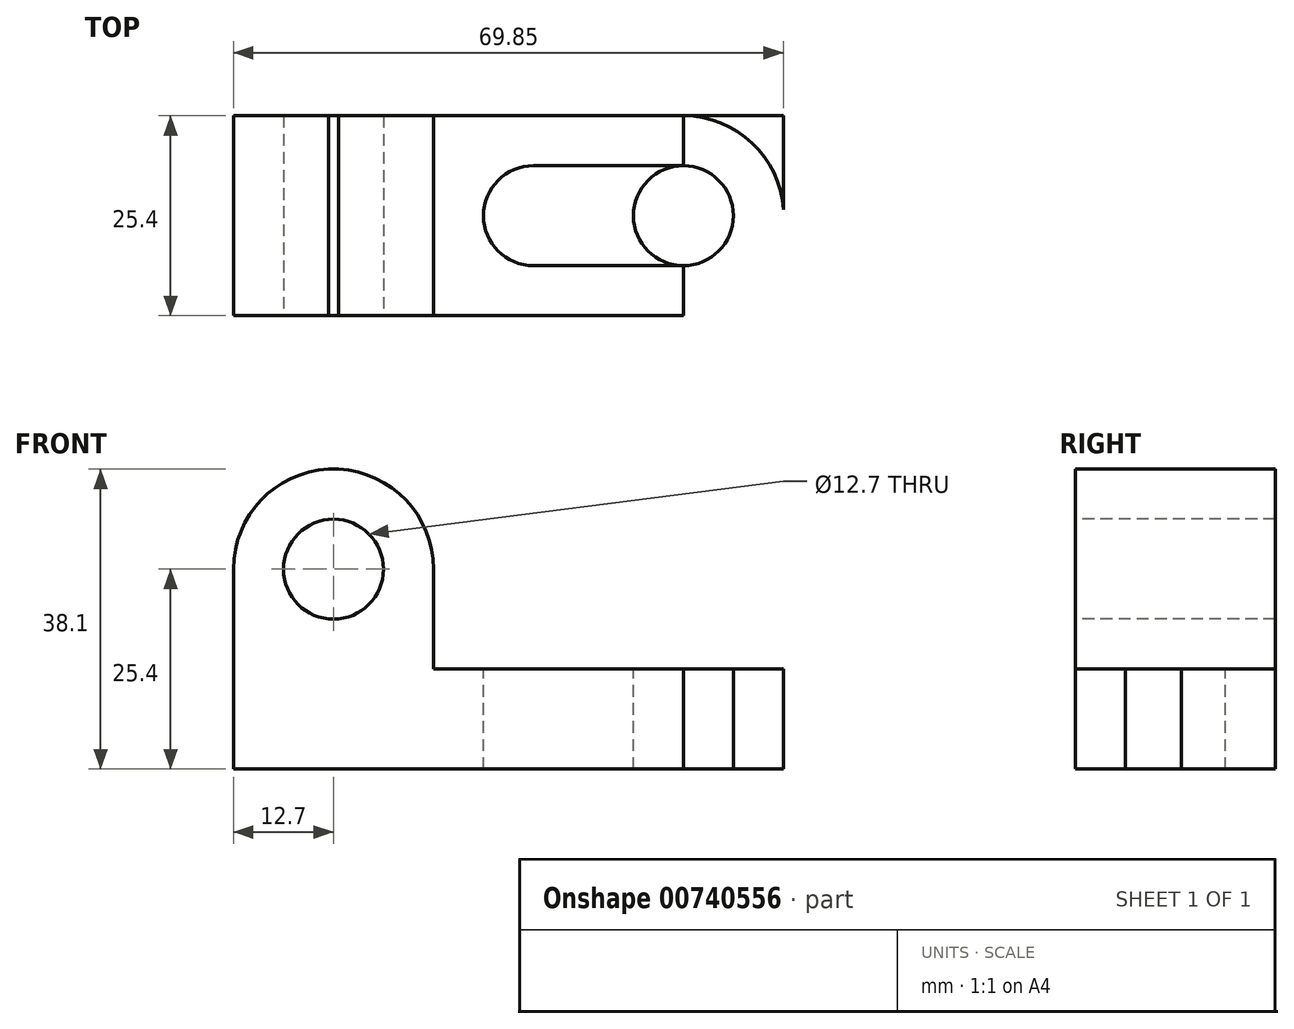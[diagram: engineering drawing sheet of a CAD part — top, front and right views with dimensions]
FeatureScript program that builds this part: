
annotation { "Feature Type Name" : "Feature", "Feature Type Description" : "" }
export const myFeature = defineFeature(function(context is Context, id is Id, definition is map)
    precondition{}
    {
        {
            var Q0;
            Q0=qCreatedBy(makeId("Front.planeOp"),FACE);
            var sketch = newSketch(context, id + "F0", { "sketchPlane" : qUnion([Q0])});
            skLineSegment(sketch, "E0", {"start": v(0, 0) * mm, "end": v(0, 38.1) * mm});
            skLineSegment(sketch, "E1", {"start": v(0, 38.1) * mm, "end": v(25.4, 38.1) * mm});
            skLineSegment(sketch, "E2", {"start": v(25.4, 38.1) * mm, "end": v(25.4, 12.7) * mm});
            skLineSegment(sketch, "E3", {"start": v(25.4, 12.7) * mm, "end": v(69.85, 12.7) * mm});
            skLineSegment(sketch, "E4", {"start": v(69.85, 12.7) * mm, "end": v(69.85, 0) * mm});
            skLineSegment(sketch, "E5", {"start": v(69.85, 0) * mm, "end": v(0, 0) * mm});
            skSolve(sketch);
        }
        {
            var Q0;
            Q0 = qSketchRegion(id + "F0", true);
            extrude(context, id + "F1", {"entities" : qUnion([Q0]), "depth" : 25.4 * mm, "offsetDistance" : 25.4 * mm});
        }
        {
            var Q0;
            Q0=makeQuery(id+"F1.opExtrude","CAP_FACE",FACE,{"disambiguationData":[OSD([sQuery(id+"F0.wireOp",EDGE,"E0"),sQuery(id+"F0.wireOp",EDGE,"E1"),sQuery(id+"F0.wireOp",EDGE,"E2"),sQuery(id+"F0.wireOp",EDGE,"E3"),sQuery(id+"F0.wireOp",EDGE,"E4"),sQuery(id+"F0.wireOp",EDGE,"E5")])],"isStart":false});
            var sketch = newSketch(context, id + "F2", { "sketchPlane" : qUnion([Q0])});
            skLineSegment(sketch, "E6", {"start": v(0, 25.4) * mm, "end": v(25.4, 25.4) * mm});
            skCircle(sketch, "E7", {"center": v(12.7, 25.4) * mm, "radius": 6.35 * mm});
            skArc(sketch, "E8", {"start": v(25.4, 25.4) * mm, "mid": v(12.7, 38.12) * mm, "end": v(0, 25.4) * mm});
            skSolve(sketch);
        }
        {
            var Q0;
            {var subQ0=sQuery(id+"F2.wireOp",EDGE,"E7");var subQ1=sQuery(id+"F2.wireOp",EDGE,"E6");var subQ2=makeQuery(id+"F2.imprint","INTERSECT",VERTEX,{"disambiguationData":[OD(0.0)],"derivedFrom":[subQ1,subQ0]});Q0=makeQuery(id+"F2.imprint","IMPRINT",FACE,{"disambiguationData":[TD([[makeQuery(id+"F2.imprint","IMPRINT",EDGE,{"disambiguationData":[TD([[subQ2,-1.0]])],"derivedFrom":subQ1}),1.0]])]});}
            var Q1;
            {var subQ0=sQuery(id+"F2.wireOp",EDGE,"E7");var subQ1=sQuery(id+"F2.wireOp",EDGE,"E6");var subQ2=makeQuery(id+"F2.imprint","INTERSECT",VERTEX,{"disambiguationData":[OD(0.0)],"derivedFrom":[subQ1,subQ0]});Q1=makeQuery(id+"F2.imprint","IMPRINT",FACE,{"disambiguationData":[TD([[makeQuery(id+"F2.imprint","IMPRINT",EDGE,{"disambiguationData":[TD([[subQ2,-1.0]])],"derivedFrom":subQ1}),-1.0]])]});}
            var Q2;
            {var subQ0=sQuery(id+"F2.wireOp",EDGE,"E8");var subQ3=makeQuery(id+"F1.opExtrude","CAP_EDGE",EDGE,{"disambiguationData":[OSD([sQuery(id+"F0.wireOp",EDGE,"E1")])],"isStart":false});var subQ4=makeQuery(id+"F2.imprint","INTERSECT",VERTEX,{"disambiguationData":[OD(1.0)],"derivedFrom":[subQ3,subQ0]});Q2=makeQuery(id+"F2.imprint","IMPRINT",FACE,{"disambiguationData":[TD([[makeQuery(id+"F2.imprint","IMPRINT",EDGE,{"disambiguationData":[TD([[subQ4,-1.0]])],"derivedFrom":subQ0}),-1.0]])]});}
            var Q3;
            {var subQ0=sQuery(id+"F2.wireOp",EDGE,"E8");var subQ3=makeQuery(id+"F1.opExtrude","CAP_EDGE",EDGE,{"disambiguationData":[OSD([sQuery(id+"F0.wireOp",EDGE,"E1")])],"isStart":false});var subQ4=makeQuery(id+"F2.imprint","INTERSECT",VERTEX,{"disambiguationData":[OD(0.0)],"derivedFrom":[subQ3,subQ0]});Q3=makeQuery(id+"F2.imprint","IMPRINT",FACE,{"disambiguationData":[TD([[makeQuery(id+"F2.imprint","IMPRINT",EDGE,{"disambiguationData":[TD([[subQ4,1.0]])],"derivedFrom":subQ0}),-1.0]])]});}
            extrude(context, id + "F3", {"entities" : qUnion([Q0, Q1, Q2, Q3]), "operationType" : NewBodyOperationType.REMOVE, "endBound" : BoundingType.THROUGH_ALL, "oppositeDirection" : true, "depth" : 25.4 * mm, "offsetDistance" : 25.4 * mm});
        }
        {
            var Q0;
            Q0=makeQuery(id+"F1.opExtrude","SWEPT_FACE",FACE,{"disambiguationData":[OSD([sQuery(id+"F0.wireOp",EDGE,"E3")])]});
            var sketch = newSketch(context, id + "F4", { "sketchPlane" : qUnion([Q0])});
            skLineSegment(sketch, "E9", {"start": v(38.1, 0) * mm, "end": v(38.1, -25.4) * mm});
            skLineSegment(sketch, "E10", {"start": v(57.15, 0) * mm, "end": v(57.15, -25.4) * mm});
            skCircle(sketch, "E11", {"center": v(38.1, -12.7) * mm, "radius": 6.35 * mm});
            skCircle(sketch, "E12", {"center": v(57.15, -12.7) * mm, "radius": 6.35 * mm});
            skLineSegment(sketch, "E13", {"start": v(38.1, -6.35) * mm, "end": v(57.15, -6.35) * mm});
            skLineSegment(sketch, "E14", {"start": v(57.15, -6.35) * mm, "end": v(57.15, -19.05) * mm});
            skLineSegment(sketch, "E15", {"start": v(57.15, -19.05) * mm, "end": v(38.1, -19.05) * mm});
            skArc(sketch, "E16", {"start": v(57.15, -25.4) * mm, "mid": v(69.87, -12.7) * mm, "end": v(57.15, 0) * mm});
            skSolve(sketch);
        }
        {
            var Q0;
            {var subQ0=sQuery(id+"F4.wireOp",EDGE,"E11");var subQ1=sQuery(id+"F4.wireOp",EDGE,"E9");var subQ2=makeQuery(id+"F4.imprint","INTERSECT",VERTEX,{"derivedFrom":[subQ1,subQ0,sQuery(id+"F4.wireOp",EDGE,"E13")]});Q0=makeQuery(id+"F4.imprint","IMPRINT",FACE,{"disambiguationData":[TD([[makeQuery(id+"F4.imprint","IMPRINT",EDGE,{"disambiguationData":[TD([[subQ2,-1.0]])],"derivedFrom":subQ1}),-1.0]])]});}
            var Q1;
            {var subQ0=sQuery(id+"F4.wireOp",EDGE,"E11");var subQ1=sQuery(id+"F4.wireOp",EDGE,"E9");var subQ2=makeQuery(id+"F4.imprint","INTERSECT",VERTEX,{"derivedFrom":[subQ1,subQ0,sQuery(id+"F4.wireOp",EDGE,"E13")]});Q1=makeQuery(id+"F4.imprint","IMPRINT",FACE,{"disambiguationData":[TD([[makeQuery(id+"F4.imprint","IMPRINT",EDGE,{"disambiguationData":[TD([[subQ2,-1.0]])],"derivedFrom":subQ1}),1.0]])]});}
            var Q2;
            {var subQ0=sQuery(id+"F4.wireOp",EDGE,"E14");Q2=makeQuery(id+"F4.imprint","IMPRINT",FACE,{"disambiguationData":[TD([[makeQuery(id+"F4.imprint","IMPRINT",EDGE,{"derivedFrom":subQ0}),-1.0]])]});}
            var Q3;
            {var subQ0=sQuery(id+"F4.wireOp",EDGE,"E14");Q3=makeQuery(id+"F4.imprint","IMPRINT",FACE,{"disambiguationData":[TD([[makeQuery(id+"F4.imprint","IMPRINT",EDGE,{"derivedFrom":subQ0}),1.0]])]});}
            var Q4;
            {var subQ0=sQuery(id+"F4.wireOp",EDGE,"E13");Q4=makeQuery(id+"F4.imprint","IMPRINT",FACE,{"disambiguationData":[TD([[makeQuery(id+"F4.imprint","IMPRINT",EDGE,{"derivedFrom":subQ0}),-1.0]])]});}
            var Q5;
            {var subQ0=sQuery(id+"F4.wireOp",EDGE,"E16");var subQ1=makeQuery(id+"F1.opExtrude","SWEPT_EDGE",EDGE,{"disambiguationData":[OSD([sQuery(id+"F0.wireOp",EDGE,"E3"),sQuery(id+"F0.wireOp",EDGE,"E4")])]});var subQ2=makeQuery(id+"F4.imprint","INTERSECT",VERTEX,{"disambiguationData":[OD(0.0)],"derivedFrom":[subQ1,subQ0]});Q5=makeQuery(id+"F4.imprint","IMPRINT",FACE,{"disambiguationData":[TD([[makeQuery(id+"F4.imprint","IMPRINT",EDGE,{"disambiguationData":[TD([[subQ2,-1.0]])],"derivedFrom":subQ0}),1.0]])]});}
            var Q6;
            {var subQ0=sQuery(id+"F4.wireOp",EDGE,"E16");var subQ1=sQuery(id+"F0.wireOp",EDGE,"E3");var subQ2=makeQuery(id+"F1.opExtrude","CAP_EDGE",EDGE,{"disambiguationData":[OSD([subQ1])],"isStart":false});var subQ3=makeQuery(id+"F4.imprint","INTERSECT",VERTEX,{"derivedFrom":[subQ2,subQ0]});Q6=makeQuery(id+"F4.imprint","IMPRINT",FACE,{"disambiguationData":[TD([[makeQuery(id+"F4.imprint","IMPRINT",EDGE,{"disambiguationData":[TD([[subQ3,-1.0]])],"derivedFrom":subQ0}),-1.0]])]});}
            var Q7;
            {var subQ0=sQuery(id+"F4.wireOp",EDGE,"E16");var subQ1=sQuery(id+"F0.wireOp",EDGE,"E3");var subQ4=makeQuery(id+"F1.opExtrude","SWEPT_EDGE",EDGE,{"disambiguationData":[OSD([subQ1,sQuery(id+"F0.wireOp",EDGE,"E4")])]});var subQ5=makeQuery(id+"F4.imprint","INTERSECT",VERTEX,{"disambiguationData":[OD(1.0)],"derivedFrom":[subQ4,subQ0]});Q7=makeQuery(id+"F4.imprint","IMPRINT",FACE,{"disambiguationData":[TD([[makeQuery(id+"F4.imprint","IMPRINT",EDGE,{"disambiguationData":[TD([[subQ5,-1.0]])],"derivedFrom":subQ0}),-1.0]])]});}
            extrude(context, id + "F5", {"entities" : qUnion([Q0, Q1, Q2, Q3, Q4, Q5, Q6, Q7]), "operationType" : NewBodyOperationType.REMOVE, "endBound" : BoundingType.THROUGH_ALL, "oppositeDirection" : true, "depth" : 25.4 * mm, "offsetDistance" : 25.4 * mm});
        }
    });
